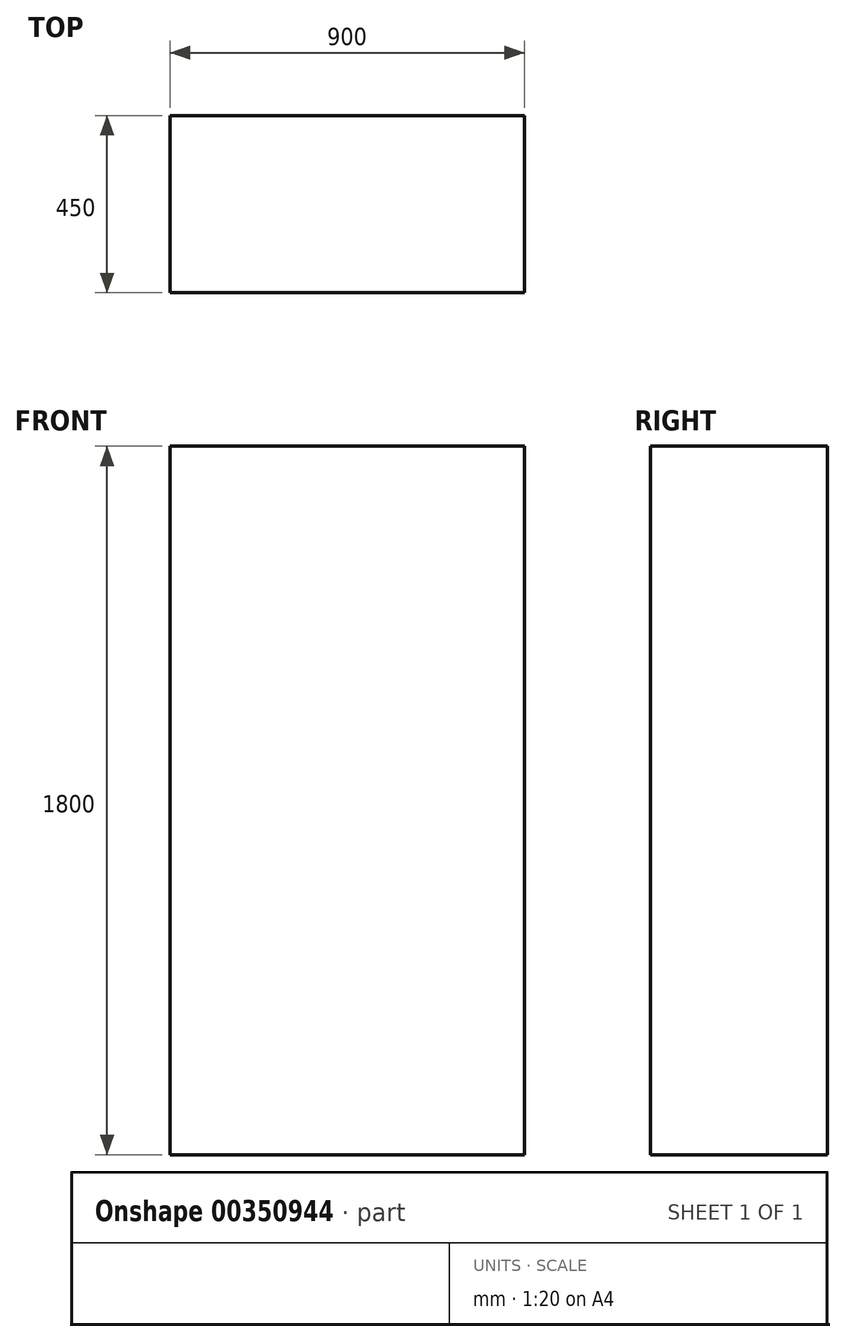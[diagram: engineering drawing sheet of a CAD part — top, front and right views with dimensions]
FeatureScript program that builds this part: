
annotation { "Feature Type Name" : "Feature", "Feature Type Description" : "" }
export const myFeature = defineFeature(function(context is Context, id is Id, definition is map)
    precondition{}
    {
        {
            var Q0;
            Q0=qCreatedBy(makeId("Front.planeOp"),FACE);
            var sketch = newSketch(context, id + "F0", { "sketchPlane" : qUnion([Q0])});
            skLineSegment(sketch, "E0.bottom", {"start": v(-450, 900) * mm, "end": v(450, 900) * mm});
            skLineSegment(sketch, "E0.top", {"start": v(-450, -900) * mm, "end": v(450, -900) * mm});
            skLineSegment(sketch, "E0.left", {"start": v(-450, 900) * mm, "end": v(-450, -900) * mm});
            skLineSegment(sketch, "E0.right", {"start": v(450, 900) * mm, "end": v(450, -900) * mm});
            skPoint(sketch, "E0.middle", {"position": v(0, 0) * mm});
            skSolve(sketch);
        }
        {
            var Q0;
            Q0 = qSketchRegion(id + "F0", true);
            extrude(context, id + "F1", {"entities" : qUnion([Q0]), "depth" : 450 * mm});
        }
    });
